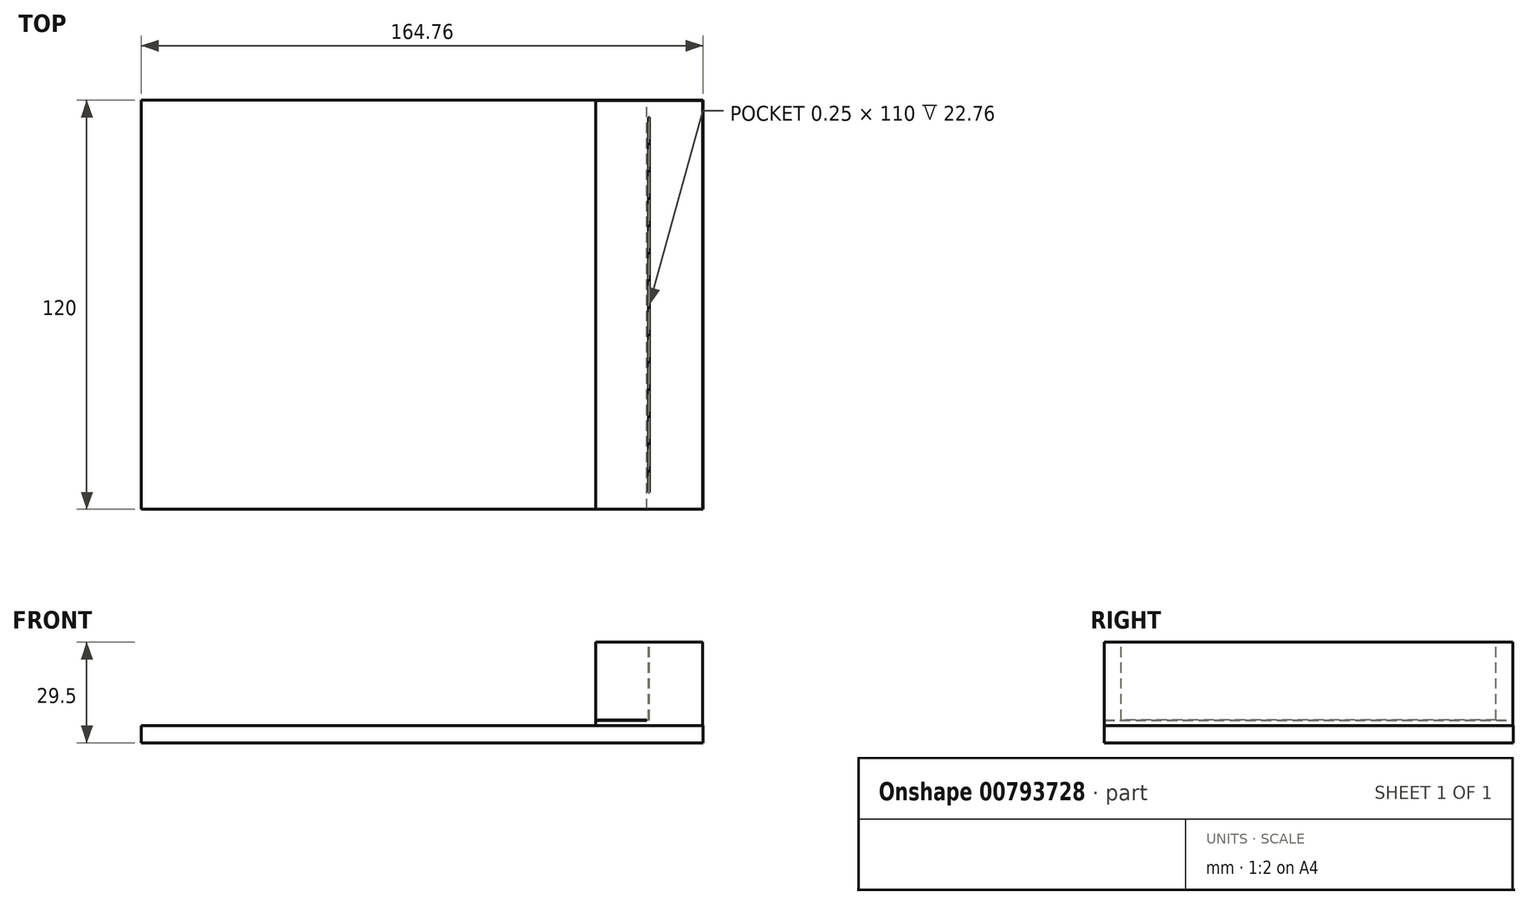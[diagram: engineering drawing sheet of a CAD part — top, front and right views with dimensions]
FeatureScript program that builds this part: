
annotation { "Feature Type Name" : "Feature", "Feature Type Description" : "" }
export const myFeature = defineFeature(function(context is Context, id is Id, definition is map)
    precondition{}
    {
        {
            var Q0;
            Q0=qCreatedBy(makeId("Top.planeOp"),FACE);
            var sketch = newSketch(context, id + "F0", { "sketchPlane" : qUnion([Q0])});
            skLineSegment(sketch, "E0.bottom", {"start": v(-82.38, 60) * mm, "end": v(82.38, 60) * mm});
            skLineSegment(sketch, "E0.top", {"start": v(-82.38, -60) * mm, "end": v(82.38, -60) * mm});
            skLineSegment(sketch, "E0.left", {"start": v(-82.38, 60) * mm, "end": v(-82.38, -60) * mm});
            skLineSegment(sketch, "E0.right", {"start": v(82.38, 60) * mm, "end": v(82.38, -60) * mm});
            skPoint(sketch, "E0.middle", {"position": v(0, 0) * mm});
            skSolve(sketch);
        }
        {
            var Q0;
            Q0 = qSketchRegion(id + "F0", true);
            extrude(context, id + "F1", {"entities" : qUnion([Q0]), "depth" : 5 * mm, "offsetDistance" : 25.4 * mm});
        }
        {
            var Q0;
            Q0=qCreatedBy(makeId("Top.planeOp"),FACE);
            var sketch = newSketch(context, id + "F2", { "sketchPlane" : qUnion([Q0])});
            skLineSegment(sketch, "E1.bottom", {"start": v(50.93, 59.96) * mm, "end": v(82.27, 59.96) * mm});
            skLineSegment(sketch, "E1.top", {"start": v(50.93, -59.96) * mm, "end": v(82.27, -59.96) * mm});
            skLineSegment(sketch, "E1.left", {"start": v(50.93, 59.96) * mm, "end": v(50.93, -59.96) * mm});
            skLineSegment(sketch, "E1.right", {"start": v(82.27, 59.96) * mm, "end": v(82.27, -59.96) * mm});
            skPoint(sketch, "E1.middle", {"position": v(66.6, 0) * mm});
            skSolve(sketch);
        }
        {
            var Q0;
            Q0 = qSketchRegion(id + "F2", true);
            extrude(context, id + "F3", {"entities" : qUnion([Q0]), "operationType" : NewBodyOperationType.ADD, "depth" : 29.5 * mm, "offsetDistance" : 25 * mm});
        }
        {
            var Q0;
            Q0=makeQuery(id+"F3.opExtrude","SWEPT_FACE",FACE,{"disambiguationData":[OSD([sQuery(id+"F2.wireOp",EDGE,"E1.left")])]});
            var sketch = newSketch(context, id + "F4", { "sketchPlane" : qUnion([Q0])});
            skLineSegment(sketch, "E2.bottom", {"start": v(60, 6.5) * mm, "end": v(-60, 6.5) * mm});
            skLineSegment(sketch, "E2.top", {"start": v(60, 6.75) * mm, "end": v(-60, 6.75) * mm});
            skLineSegment(sketch, "E2.left", {"start": v(60, 6.5) * mm, "end": v(60, 6.75) * mm});
            skLineSegment(sketch, "E2.right", {"start": v(-60, 6.5) * mm, "end": v(-60, 6.75) * mm});
            skPoint(sketch, "E2.middle", {"position": v(0, 6.62) * mm});
            skSolve(sketch);
        }
        {
            var Q0;
            {var subQ0=sQuery(id+"F4.wireOp",EDGE,"E2.bottom");var subQ1=sQuery(id+"F2.wireOp",EDGE,"E1.left");var subQ2=makeQuery(id+"F3.opExtrude","SWEPT_EDGE",EDGE,{"disambiguationData":[OSD([sQuery(id+"F2.wireOp",EDGE,"E1.top"),subQ1])]});var subQ3=makeQuery(id+"F4.imprint","INTERSECT",VERTEX,{"derivedFrom":[subQ2,subQ0]});Q0=makeQuery(id+"F4.imprint","IMPRINT",FACE,{"disambiguationData":[TD([[makeQuery(id+"F4.imprint","IMPRINT",EDGE,{"disambiguationData":[TD([[subQ3,-1.0]])],"derivedFrom":subQ0}),-1.0]])]});}
            extrude(context, id + "F5", {"entities" : qUnion([Q0]), "operationType" : NewBodyOperationType.REMOVE, "oppositeDirection" : true, "depth" : 15 * mm, "offsetDistance" : 25 * mm});
        }
        {
            var Q0;
            Q0=makeQuery(id+"F3.opExtrude","CAP_FACE",FACE,{"disambiguationData":[OSD([sQuery(id+"F2.wireOp",EDGE,"E1.bottom"),sQuery(id+"F2.wireOp",EDGE,"E1.top"),sQuery(id+"F2.wireOp",EDGE,"E1.left"),sQuery(id+"F2.wireOp",EDGE,"E1.right")])],"isStart":false});
            var sketch = newSketch(context, id + "F6", { "sketchPlane" : qUnion([Q0])});
            skLineSegment(sketch, "E3.bottom", {"start": v(66.72, 55) * mm, "end": v(66.47, 55) * mm});
            skLineSegment(sketch, "E3.top", {"start": v(66.72, -55) * mm, "end": v(66.47, -55) * mm});
            skLineSegment(sketch, "E3.left", {"start": v(66.72, 55) * mm, "end": v(66.72, -55) * mm});
            skLineSegment(sketch, "E3.right", {"start": v(66.47, 55) * mm, "end": v(66.47, -55) * mm});
            skPoint(sketch, "E3.middle", {"position": v(66.6, 0) * mm});
            skPoint(sketch, "E3.middle.positionSnap0", {"position": v(82.27, 0) * mm});
            skPoint(sketch, "E3.middle.positionSnap1", {"position": v(66.6, 59.96) * mm});
            skPoint(sketch, "E3.centerSnap0", {"position": v(82.27, 0) * mm});
            skPoint(sketch, "E3.centerSnap1", {"position": v(66.6, 59.96) * mm});
            skSolve(sketch);
        }
        {
            var Q0;
            Q0=makeQuery(id+"F6.imprint","IMPRINT",FACE,{"disambiguationData":[TD([[makeQuery(id+"F6.imprint","IMPRINT",EDGE,{"derivedFrom":sQuery(id+"F6.wireOp",EDGE,"E3.bottom")}),1.0]])]});
            extrude(context, id + "F7", {"entities" : qUnion([Q0]), "operationType" : NewBodyOperationType.REMOVE, "oppositeDirection" : true, "depth" : 22.76 * mm, "offsetDistance" : 25 * mm});
        }
    });
